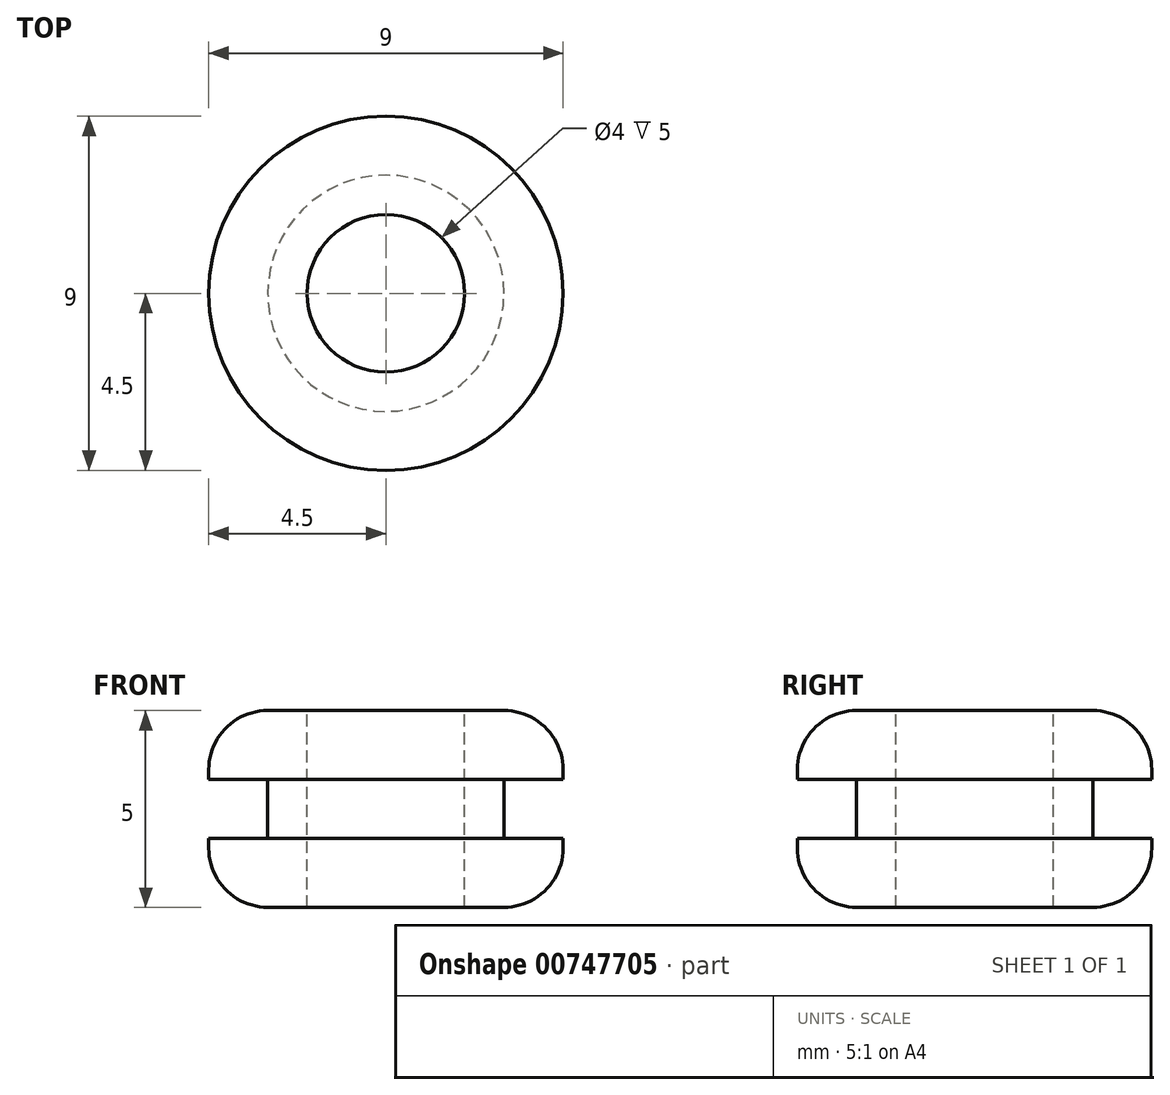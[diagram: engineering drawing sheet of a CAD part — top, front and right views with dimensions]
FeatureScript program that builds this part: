
annotation { "Feature Type Name" : "Feature", "Feature Type Description" : "" }
export const myFeature = defineFeature(function(context is Context, id is Id, definition is map)
    precondition{}
    {
        {
            var Q0;
            Q0=qCreatedBy(makeId("Front.planeOp"),FACE);
            var sketch = newSketch(context, id + "F0", { "sketchPlane" : qUnion([Q0])});
            skLineSegment(sketch, "E0", {"start": v(0, 0) * mm, "end": v(0, 2.5) * mm});
            skLineSegment(sketch, "E1", {"start": v(0, 2.5) * mm, "end": v(3, 2.5) * mm});
            skLineSegment(sketch, "E2", {"start": v(4.5, 1) * mm, "end": v(4.5, 0.75) * mm});
            skLineSegment(sketch, "E3", {"start": v(4.5, 0.75) * mm, "end": v(3, 0.75) * mm});
            skLineSegment(sketch, "E4", {"start": v(3, 0.75) * mm, "end": v(3, -0.75) * mm});
            skLineSegment(sketch, "E5", {"start": v(3, -0.75) * mm, "end": v(4.5, -0.75) * mm});
            skLineSegment(sketch, "E6", {"start": v(4.5, -0.75) * mm, "end": v(4.5, -1) * mm});
            skLineSegment(sketch, "E7", {"start": v(3, -2.5) * mm, "end": v(0, -2.5) * mm});
            skLineSegment(sketch, "E8", {"start": v(0, -2.5) * mm, "end": v(0, 0) * mm});
            skPoint(sketch, "E9.visualSharp", {"position": v(4.5, 2.5) * mm});
            skArc(sketch, "E9.filletArc", {"start": v(4.5, 1) * mm, "mid": v(4.06, 2.06) * mm, "end": v(3, 2.5) * mm});
            skPoint(sketch, "E10.visualSharp", {"position": v(4.5, -2.5) * mm});
            skArc(sketch, "E10.filletArc", {"start": v(3, -2.5) * mm, "mid": v(4.06, -2.06) * mm, "end": v(4.5, -1) * mm});
            skSolve(sketch);
        }
        {
            var Q0;
            Q0 = qSketchRegion(id + "F0", true);
            var Q1;
            Q1=sQuery(id+"F0.wireOp",EDGE,"E0");
            revolve(context, id + "F1", {"surfaceOperationType" : NewSurfaceOperationType.NEW, "entities" : qUnion([Q0]), "axis" : qUnion([Q1]), "revolveType" : RevolveType.FULL});
        }
        {
            var Q0;
            Q0=makeQuery(id+"F1.opRevolve","SWEPT_FACE",FACE,{"disambiguationData":[OSD([sQuery(id+"F0.wireOp",EDGE,"E1")])]});
            var sketch = newSketch(context, id + "F2", { "sketchPlane" : qUnion([Q0])});
            skCircle(sketch, "E11", {"center": v(0, 0) * mm, "radius": 2 * mm});
            skSolve(sketch);
        }
        {
            var Q0;
            Q0 = qSketchRegion(id + "F2", true);
            var Q1;
            Q1=makeQuery(id+"F1.opRevolve","SWEPT_FACE",FACE,{"disambiguationData":[OSD([sQuery(id+"F0.wireOp",EDGE,"E7")])]});
            extrude(context, id + "F3", {"entities" : qUnion([Q0]), "operationType" : NewBodyOperationType.REMOVE, "endBound" : BoundingType.UP_TO_SURFACE, "oppositeDirection" : true, "depth" : 25 * mm, "endBoundEntityFace" : qUnion([Q1]), "offsetDistance" : 25 * mm});
        }
    });
